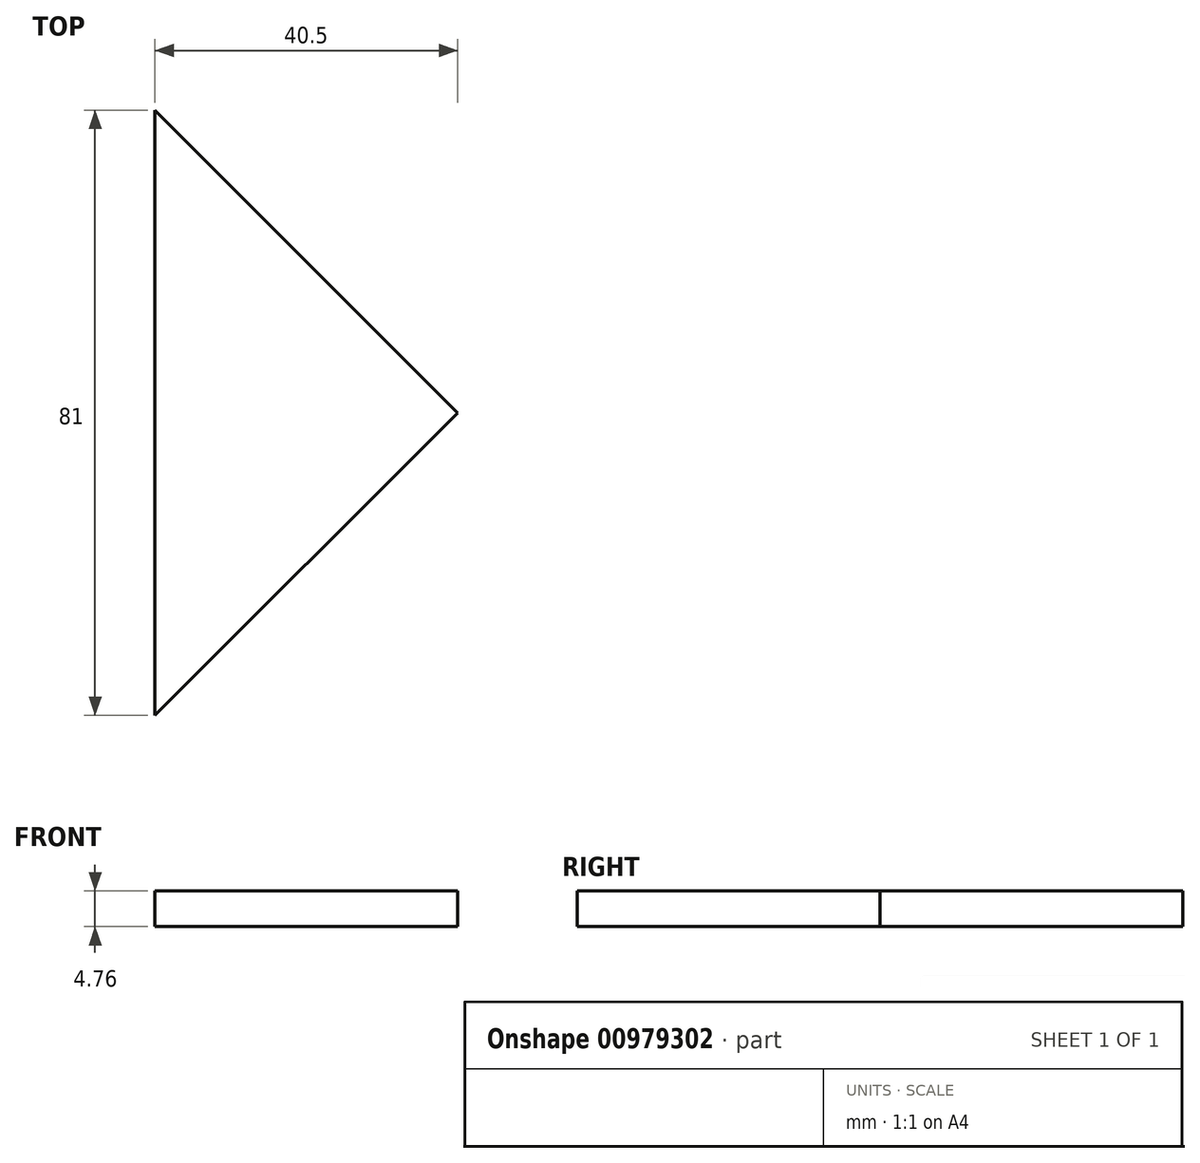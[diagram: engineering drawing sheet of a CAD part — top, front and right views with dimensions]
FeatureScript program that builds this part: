
annotation { "Feature Type Name" : "Feature", "Feature Type Description" : "" }
export const myFeature = defineFeature(function(context is Context, id is Id, definition is map)
    precondition{}
    {
        {
            var Q0;
            Q0=qCreatedBy(makeId("Top.planeOp"),FACE);
            var sketch = newSketch(context, id + "F0", { "sketchPlane" : qUnion([Q0])});
            skLineSegment(sketch, "E0.bottom", {"start": v(-40.5, 40.5) * mm, "end": v(40.5, 40.5) * mm});
            skLineSegment(sketch, "E0.top", {"start": v(-40.5, -40.5) * mm, "end": v(40.5, -40.5) * mm});
            skLineSegment(sketch, "E0.left", {"start": v(-40.5, 40.5) * mm, "end": v(-40.5, -40.5) * mm});
            skLineSegment(sketch, "E0.right", {"start": v(40.5, 40.5) * mm, "end": v(40.5, -40.5) * mm});
            skPoint(sketch, "E0.middle", {"position": v(0, 0) * mm});
            skLineSegment(sketch, "E1", {"start": v(-40.5, 40.5) * mm, "end": v(40.5, -40.5) * mm});
            skLineSegment(sketch, "E2", {"start": v(40.5, 40.5) * mm, "end": v(-40.5, -40.5) * mm});
            skSolve(sketch);
        }
        {
            var Q0;
            {var subQ0=sQuery(id+"F0.wireOp",EDGE,"E0.left");Q0=makeQuery(id+"F0.imprint","IMPRINT",FACE,{"disambiguationData":[TD([[makeQuery(id+"F0.imprint","IMPRINT",EDGE,{"derivedFrom":subQ0}),1.0]])]});}
            extrude(context, id + "F1", {"entities" : qUnion([Q0]), "depth" : 4.76 * mm, "offsetDistance" : 25 * mm});
        }
    });
